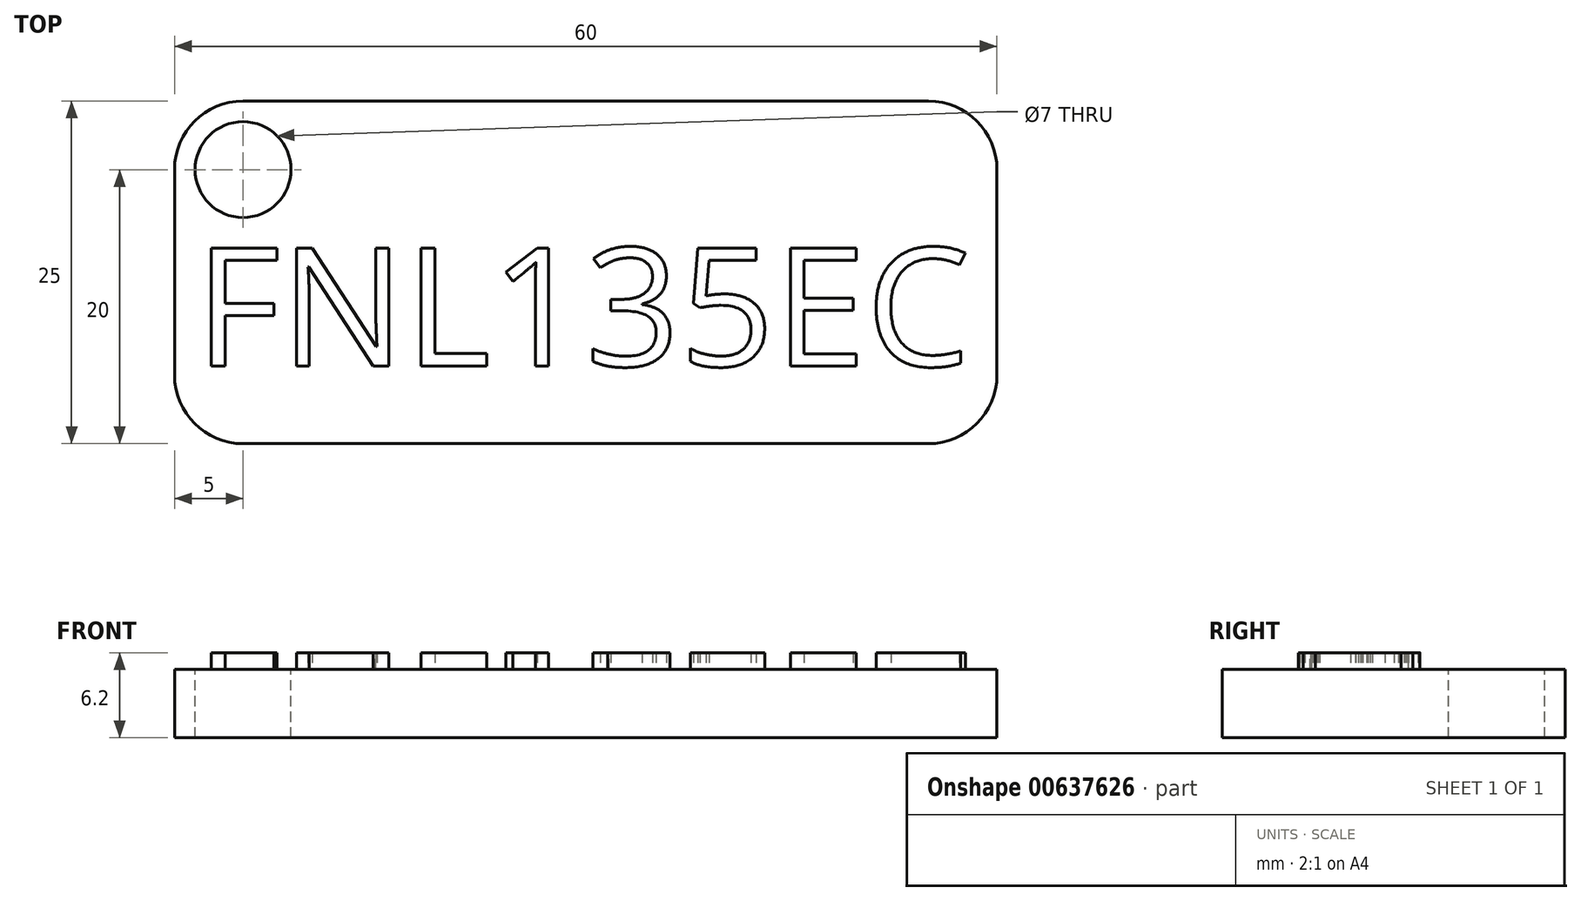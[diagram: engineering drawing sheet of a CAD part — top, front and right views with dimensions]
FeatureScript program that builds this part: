
annotation { "Feature Type Name" : "Feature", "Feature Type Description" : "" }
export const myFeature = defineFeature(function(context is Context, id is Id, definition is map)
    precondition{}
    {
        {
            var Q0;
            Q0=qCreatedBy(makeId("Top.planeOp"),FACE);
            var sketch = newSketch(context, id + "F0", { "sketchPlane" : qUnion([Q0])});
            skLineSegment(sketch, "E0.bottom", {"start": v(30, 12.5) * mm, "end": v(-30, 12.5) * mm});
            skLineSegment(sketch, "E0.top", {"start": v(30, -12.5) * mm, "end": v(-30, -12.5) * mm});
            skLineSegment(sketch, "E0.left", {"start": v(30, 12.5) * mm, "end": v(30, -12.5) * mm});
            skLineSegment(sketch, "E0.right", {"start": v(-30, 12.5) * mm, "end": v(-30, -12.5) * mm});
            skPoint(sketch, "E0.middle", {"position": v(0, 0) * mm});
            skSolve(sketch);
        }
        {
            var Q0;
            Q0 = qSketchRegion(id + "F0", true);
            extrude(context, id + "F1", {"entities" : qUnion([Q0]), "depth" : 5 * mm, "offsetDistance" : 25 * mm});
        }
        {
            var Q0;
            Q0=makeQuery(id+"F1.opExtrude","CAP_FACE",FACE,{"disambiguationData":[OSD([sQuery(id+"F0.wireOp",EDGE,"E0.bottom"),sQuery(id+"F0.wireOp",EDGE,"E0.top"),sQuery(id+"F0.wireOp",EDGE,"E0.left"),sQuery(id+"F0.wireOp",EDGE,"E0.right")])],"isStart":false});
            var sketch = newSketch(context, id + "F2", { "sketchPlane" : qUnion([Q0])});
            skPoint(sketch, "E1", {"position": v(-25, 7.5) * mm});
            skSolve(sketch);
        }
        {
            var Q0;
            Q0=sQuery(id+"F2.wireOp",VERTEX,"E1");
            var Q1;
            Q1=makeQuery(id+"F1.opExtrude","SWEPT_BODY",BODY,{"disambiguationData":[OSD([sQuery(id+"F0.wireOp",EDGE,"E0.bottom"),sQuery(id+"F0.wireOp",EDGE,"E0.top"),sQuery(id+"F0.wireOp",EDGE,"E0.left"),sQuery(id+"F0.wireOp",EDGE,"E0.right")])]});
            hole(context, id + "F3", {"style" : HoleStyle.SIMPLE, "endStyle" : HoleEndStyle.THROUGH, "holeDiameter" : 7 * mm, "majorDiameter" : 5 * mm, "isTappedThrough" : true, "tappedDepth" : 12 * mm, "tapClearance" : 3, "locations" : qUnion([Q0]), "scope" : qUnion([Q1])});
        }
        {
            var Q0;
            Q0=makeQuery(id+"F1.opExtrude","SWEPT_EDGE",EDGE,{"disambiguationData":[OSD([sQuery(id+"F0.wireOp",EDGE,"E0.top"),sQuery(id+"F0.wireOp",EDGE,"E0.left")])]});
            var Q1;
            Q1=makeQuery(id+"F1.opExtrude","SWEPT_EDGE",EDGE,{"disambiguationData":[OSD([sQuery(id+"F0.wireOp",EDGE,"E0.top"),sQuery(id+"F0.wireOp",EDGE,"E0.right")])]});
            var Q2;
            Q2=makeQuery(id+"F1.opExtrude","SWEPT_EDGE",EDGE,{"disambiguationData":[OSD([sQuery(id+"F0.wireOp",EDGE,"E0.bottom"),sQuery(id+"F0.wireOp",EDGE,"E0.right")])]});
            var Q3;
            Q3=makeQuery(id+"F1.opExtrude","SWEPT_EDGE",EDGE,{"disambiguationData":[OSD([sQuery(id+"F0.wireOp",EDGE,"E0.bottom"),sQuery(id+"F0.wireOp",EDGE,"E0.left")])]});
            fillet(context, id + "F4", {"entities" : qUnion([Q0, Q1, Q2, Q3]), "radius" : 5 * mm, "tangentPropagation" : true, "allowEdgeOverflow" : false});
        }
        {
            var Q0;
            Q0=makeQuery(id+"F1.opExtrude","CAP_FACE",FACE,{"disambiguationData":[OSD([sQuery(id+"F0.wireOp",EDGE,"E0.bottom"),sQuery(id+"F0.wireOp",EDGE,"E0.top"),sQuery(id+"F0.wireOp",EDGE,"E0.left"),sQuery(id+"F0.wireOp",EDGE,"E0.right")])],"isStart":false});
            var sketch = newSketch(context, id + "F5", { "sketchPlane" : qUnion([Q0])});
            skPoint(sketch, "E2", {"position": v(-11.83, 0) * mm});
            skPoint(sketch, "E3", {"position": v(-11.83, 1.86) * mm});
            skPoint(sketch, "E4", {"position": v(-28.5, 1.86) * mm});
            skText(sketch, "E5", { "text": "FNL135EC", "fontName": "OpenSans-Regular.ttf"});
            const initialGuessF5  = {"E5": [-0.0285, -0.00683, 1, 0, 0.00868]};
            skSetInitialGuess(sketch, initialGuessF5);
            skSolve(sketch);
        }
        {
            var Q0;
            Q0 = qSketchRegion(id + "F5", true);
            extrude(context, id + "F6", {"entities" : qUnion([Q0]), "operationType" : NewBodyOperationType.ADD, "depth" : 1.2 * mm, "offsetDistance" : 25 * mm});
        }
    });
